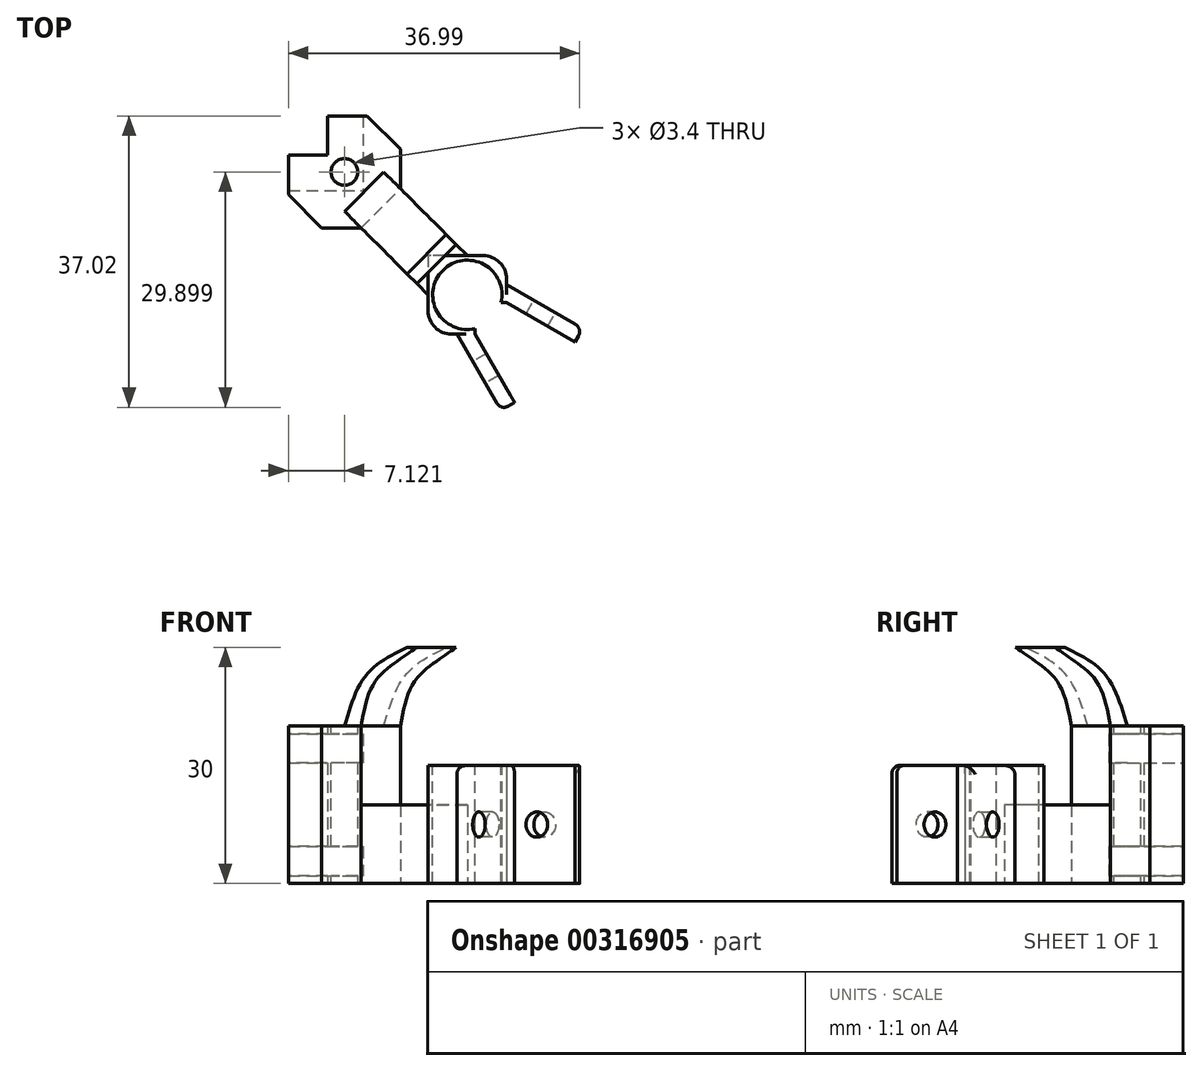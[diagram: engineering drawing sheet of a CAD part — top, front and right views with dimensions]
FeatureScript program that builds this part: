
annotation { "Feature Type Name" : "Feature", "Feature Type Description" : "" }
export const myFeature = defineFeature(function(context is Context, id is Id, definition is map)
    precondition{}
    {
        {
            var Q0;
            Q0=qCreatedBy(makeId("Top.planeOp"),FACE);
            var sketch = newSketch(context, id + "F0", { "sketchPlane" : qUnion([Q0])});
            skLineSegment(sketch, "E0", {"start": v(0, 0) * mm, "end": v(-5, 0) * mm});
            skLineSegment(sketch, "E1", {"start": v(-5, 0) * mm, "end": v(-5, 5) * mm});
            skLineSegment(sketch, "E2", {"start": v(-5, 5) * mm, "end": v(0, 5) * mm});
            skLineSegment(sketch, "E3", {"start": v(0, 5) * mm, "end": v(0, 10) * mm});
            skLineSegment(sketch, "E4", {"start": v(0, 10) * mm, "end": v(5, 10) * mm});
            skLineSegment(sketch, "E5", {"start": v(5, 10) * mm, "end": v(5, 5) * mm});
            skLineSegment(sketch, "E6", {"start": v(-5, 0) * mm, "end": v(-0.76, -4.24) * mm});
            skLineSegment(sketch, "E7", {"start": v(5, 10) * mm, "end": v(9.24, 5.76) * mm});
            skLineSegment(sketch, "E8", {"start": v(9.24, 5.76) * mm, "end": v(9.24, 0.76) * mm});
            skLineSegment(sketch, "E9", {"start": v(-0.76, -4.24) * mm, "end": v(4.24, -4.24) * mm});
            skLineSegment(sketch, "E10", {"start": v(9.24, 0.76) * mm, "end": v(17.73, -7.73) * mm});
            skLineSegment(sketch, "E11", {"start": v(4.24, -4.24) * mm, "end": v(12.73, -12.73) * mm});
            skLineSegment(sketch, "E12", {"start": v(12.73, -12.73) * mm, "end": v(12.73, -17.73) * mm});
            skLineSegment(sketch, "E13", {"start": v(12.73, -17.73) * mm, "end": v(22.73, -17.73) * mm});
            skLineSegment(sketch, "E14", {"start": v(22.73, -17.73) * mm, "end": v(22.73, -7.73) * mm});
            skLineSegment(sketch, "E15", {"start": v(22.73, -7.73) * mm, "end": v(17.73, -7.73) * mm});
            skLineSegment(sketch, "E16", {"start": v(4.24, -4.24) * mm, "end": v(9.24, 0.76) * mm});
            skPoint(sketch, "E17", {"position": v(22.73, -13.73) * mm});
            skPoint(sketch, "E18", {"position": v(18.73, -17.73) * mm});
            skLineSegment(sketch, "E19", {"start": v(22.73, -13.73) * mm, "end": v(31.39, -18.73) * mm});
            skLineSegment(sketch, "E20", {"start": v(18.73, -17.73) * mm, "end": v(23.73, -26.39) * mm});
            skLineSegment(sketch, "E21", {"start": v(31.39, -18.73) * mm, "end": v(32.39, -17) * mm});
            skLineSegment(sketch, "E22", {"start": v(32.39, -17) * mm, "end": v(22.73, -11.42) * mm});
            skLineSegment(sketch, "E23", {"start": v(23.73, -26.39) * mm, "end": v(22, -27.39) * mm});
            skLineSegment(sketch, "E24", {"start": v(22, -27.39) * mm, "end": v(16.42, -17.73) * mm});
            skSolve(sketch);
        }
        {
            var Q0;
            Q0=makeQuery(id+"F0.imprint","IMPRINT",FACE,{"disambiguationData":[TD([[makeQuery(id+"F0.imprint","IMPRINT",EDGE,{"derivedFrom":sQuery(id+"F0.wireOp",EDGE,"E1")}),-1.0]])]});
            extrude(context, id + "F1", {"entities" : qUnion([Q0]), "depth" : 20 * mm});
        }
        {
            var Q0;
            Q0=makeQuery(id+"F0.imprint","IMPRINT",FACE,{"disambiguationData":[TD([[makeQuery(id+"F0.imprint","IMPRINT",EDGE,{"derivedFrom":sQuery(id+"F0.wireOp",EDGE,"E10")}),-1.0]])]});
            extrude(context, id + "F2", {"entities" : qUnion([Q0]), "operationType" : NewBodyOperationType.ADD, "depth" : 10 * mm});
        }
        {
            var Q0;
            Q0=makeQuery(id+"F1.opExtrude","SWEPT_FACE",FACE,{"disambiguationData":[OSD([sQuery(id+"F0.wireOp",EDGE,"E4")])]});
            var sketch = newSketch(context, id + "F3", { "sketchPlane" : qUnion([Q0])});
            skPoint(sketch, "E25", {"position": v(0, 19) * mm});
            skPoint(sketch, "E26", {"position": v(0, 15.6) * mm});
            skPoint(sketch, "E27", {"position": v(0, 1) * mm});
            skPoint(sketch, "E28", {"position": v(0, 4.4) * mm});
            skLineSegment(sketch, "E29", {"start": v(0, 19) * mm, "end": v(-5, 19) * mm});
            skLineSegment(sketch, "E30", {"start": v(-5, 19) * mm, "end": v(-5, 15.6) * mm});
            skLineSegment(sketch, "E31", {"start": v(-5, 15.6) * mm, "end": v(0, 15.6) * mm});
            skSolve(sketch);
        }
        {
            var Q0;
            Q0=qSketchRegion(id+"F3",true);
            var Q1;
            {var subQ0=sQuery(id+"F3.wireOp",EDGE,"E29");Q1=makeQuery(id+"F3.imprint","IMPRINT",FACE,{"disambiguationData":[TD([[makeQuery(id+"F3.imprint","IMPRINT",EDGE,{"derivedFrom":subQ0}),1.0]])]});}
            extrude(context, id + "F4", {"entities" : qUnion([Q0, Q1]), "operationType" : NewBodyOperationType.REMOVE, "oppositeDirection" : true, "depth" : 25 * mm});
        }
        {
            var Q0;
            Q0=makeQuery(id+"F1.opExtrude","SWEPT_FACE",FACE,{"disambiguationData":[OSD([sQuery(id+"F0.wireOp",EDGE,"E2")])]});
            var sketch = newSketch(context, id + "F5", { "sketchPlane" : qUnion([Q0])});
            skLineSegment(sketch, "E32", {"start": v(0, 19) * mm, "end": v(5, 19) * mm});
            skLineSegment(sketch, "E33", {"start": v(5, 19) * mm, "end": v(5, 15.6) * mm});
            skLineSegment(sketch, "E34", {"start": v(5, 15.6) * mm, "end": v(0, 15.6) * mm});
            skLineSegment(sketch, "E35", {"start": v(0, 15.6) * mm, "end": v(0, 19) * mm});
            skSolve(sketch);
        }
        {
            var Q0;
            Q0=makeQuery(id+"F5.imprint","IMPRINT",FACE,{"disambiguationData":[TD([[makeQuery(id+"F5.imprint","IMPRINT",EDGE,{"derivedFrom":sQuery(id+"F5.wireOp",EDGE,"E32")}),-1.0]])]});
            extrude(context, id + "F6", {"entities" : qUnion([Q0]), "operationType" : NewBodyOperationType.REMOVE, "oppositeDirection" : true, "depth" : 25 * mm});
        }
        {
            var Q0;
            Q0=makeQuery(id+"F1.opExtrude","SWEPT_FACE",FACE,{"disambiguationData":[OSD([sQuery(id+"F0.wireOp",EDGE,"E7")])]});
            var sketch = newSketch(context, id + "F7", { "sketchPlane" : qUnion([Q0])});
            skLineSegment(sketch, "E36", {"start": v(3.54, 15.6) * mm, "end": v(-2.46, 15.6) * mm});
            skLineSegment(sketch, "E37", {"start": v(-2.46, 15.6) * mm, "end": v(-2.46, 19) * mm});
            skLineSegment(sketch, "E38", {"start": v(-2.46, 19) * mm, "end": v(3.54, 19) * mm});
            skLineSegment(sketch, "E39", {"start": v(3.54, 19) * mm, "end": v(3.54, 15.6) * mm});
            skSolve(sketch);
        }
        {
            var Q0;
            Q0=qSketchRegion(id+"F7",true);
            extrude(context, id + "F8", {"entities" : qUnion([Q0]), "operationType" : NewBodyOperationType.REMOVE, "oppositeDirection" : true, "depth" : 25 * mm});
        }
        {
            var Q0;
            {var subQ3=sQuery(id+"F0.wireOp",EDGE,"E4");Q0=makeQuery(id+"F4.boolean.opBoolean","SPLIT",FACE,{"disambiguationData":[TD([makeQuery(id+"F4.opExtrude","SWEPT_FACE",FACE,{"disambiguationData":[OSD([sQuery(id+"F3.wireOp",EDGE,"E31")])]})])],"derivedFrom":makeQuery(id+"F1.opExtrude","SWEPT_FACE",FACE,{"disambiguationData":[OSD([subQ3])]})});}
            var sketch = newSketch(context, id + "F9", { "sketchPlane" : qUnion([Q0])});
            skPoint(sketch, "E40", {"position": v(0, 1) * mm});
            skPoint(sketch, "E41", {"position": v(0, 4.4) * mm});
            skLineSegment(sketch, "E42.bottom", {"start": v(0, 4.4) * mm, "end": v(-5, 4.4) * mm});
            skLineSegment(sketch, "E42.top", {"start": v(0, 1) * mm, "end": v(-5, 1) * mm});
            skLineSegment(sketch, "E42.left", {"start": v(0, 4.4) * mm, "end": v(0, 1) * mm});
            skLineSegment(sketch, "E42.right", {"start": v(-5, 4.4) * mm, "end": v(-5, 1) * mm});
            skSolve(sketch);
        }
        {
            var Q0;
            Q0=qSketchRegion(id+"F9",true);
            extrude(context, id + "F10", {"entities" : qUnion([Q0]), "operationType" : NewBodyOperationType.REMOVE, "oppositeDirection" : true, "depth" : 25 * mm});
        }
        {
            var Q0;
            {var subQ3=sQuery(id+"F0.wireOp",EDGE,"E7");Q0=makeQuery(id+"F8.boolean.opBoolean","SPLIT",FACE,{"disambiguationData":[TD([makeQuery(id+"F4.boolean.opBoolean","COPY",FACE,{"derivedFrom":makeQuery(id+"F4.opExtrude","SWEPT_FACE",FACE,{"disambiguationData":[OSD([sQuery(id+"F3.wireOp",EDGE,"E31")])]})})])],"derivedFrom":makeQuery(id+"F1.opExtrude","SWEPT_FACE",FACE,{"disambiguationData":[OSD([subQ3])]})});}
            var sketch = newSketch(context, id + "F11", { "sketchPlane" : qUnion([Q0])});
            skLineSegment(sketch, "E43.bottom", {"start": v(3.54, 1) * mm, "end": v(-2.46, 1) * mm});
            skLineSegment(sketch, "E43.top", {"start": v(3.54, 4.4) * mm, "end": v(-2.46, 4.4) * mm});
            skLineSegment(sketch, "E43.left", {"start": v(3.54, 1) * mm, "end": v(3.54, 4.4) * mm});
            skLineSegment(sketch, "E43.right", {"start": v(-2.46, 1) * mm, "end": v(-2.46, 4.4) * mm});
            skSolve(sketch);
        }
        {
            var Q0;
            Q0=qSketchRegion(id+"F11",true);
            extrude(context, id + "F12", {"entities" : qUnion([Q0]), "operationType" : NewBodyOperationType.REMOVE, "oppositeDirection" : true, "depth" : 25 * mm});
        }
        {
            var Q0;
            {var subQ2=sQuery(id+"F0.wireOp",EDGE,"E2");Q0=makeQuery(id+"F6.boolean.opBoolean","SPLIT",FACE,{"disambiguationData":[TD([makeQuery(id+"F4.boolean.opBoolean","COPY",FACE,{"derivedFrom":makeQuery(id+"F4.opExtrude","SWEPT_FACE",FACE,{"disambiguationData":[OSD([sQuery(id+"F3.wireOp",EDGE,"E31")])]})})])],"derivedFrom":makeQuery(id+"F1.opExtrude","SWEPT_FACE",FACE,{"disambiguationData":[OSD([subQ2])]})});}
            var sketch = newSketch(context, id + "F13", { "sketchPlane" : qUnion([Q0])});
            skLineSegment(sketch, "E44.bottom", {"start": v(0, 4.4) * mm, "end": v(5, 4.4) * mm});
            skLineSegment(sketch, "E44.top", {"start": v(0, 1) * mm, "end": v(5, 1) * mm});
            skLineSegment(sketch, "E44.left", {"start": v(0, 4.4) * mm, "end": v(0, 1) * mm});
            skLineSegment(sketch, "E44.right", {"start": v(5, 4.4) * mm, "end": v(5, 1) * mm});
            skSolve(sketch);
        }
        {
            var Q0;
            Q0=qSketchRegion(id+"F13",true);
            extrude(context, id + "F14", {"entities" : qUnion([Q0]), "operationType" : NewBodyOperationType.REMOVE, "oppositeDirection" : true, "depth" : 25 * mm});
        }
        {
            var Q0;
            Q0=makeQuery(id+"F1.opExtrude","CAP_FACE",FACE,{"disambiguationData":[OSD([sQuery(id+"F0.wireOp",EDGE,"E1"),sQuery(id+"F0.wireOp",EDGE,"E2"),sQuery(id+"F0.wireOp",EDGE,"E3"),sQuery(id+"F0.wireOp",EDGE,"E4"),sQuery(id+"F0.wireOp",EDGE,"E6"),sQuery(id+"F0.wireOp",EDGE,"E7"),sQuery(id+"F0.wireOp",EDGE,"E8"),sQuery(id+"F0.wireOp",EDGE,"E9"),sQuery(id+"F0.wireOp",EDGE,"E16")])],"isStart":false});
            var sketch = newSketch(context, id + "F15", { "sketchPlane" : qUnion([Q0])});
            skLineSegment(sketch, "E45", {"start": v(0, 5) * mm, "end": v(0, 3.17) * mm});
            skLineSegment(sketch, "E46", {"start": v(0, 5) * mm, "end": v(2.05, 5) * mm});
            skLineSegment(sketch, "E47", {"start": v(0, 5) * mm, "end": v(2.12, 2.88) * mm});
            skSolve(sketch);
        }
        {
            var Q0;
            Q0=sQuery(id+"F15.wireOp",VERTEX,"E47.end");
            var Q1;
            Q1=makeQuery(id+"F1.opExtrude","SWEPT_BODY",BODY,{"disambiguationData":[OSD([sQuery(id+"F0.wireOp",EDGE,"E1"),sQuery(id+"F0.wireOp",EDGE,"E2"),sQuery(id+"F0.wireOp",EDGE,"E3"),sQuery(id+"F0.wireOp",EDGE,"E4"),sQuery(id+"F0.wireOp",EDGE,"E6"),sQuery(id+"F0.wireOp",EDGE,"E7"),sQuery(id+"F0.wireOp",EDGE,"E8"),sQuery(id+"F0.wireOp",EDGE,"E9"),sQuery(id+"F0.wireOp",EDGE,"E16")])]});
            hole(context, id + "F16", {"style" : HoleStyle.SIMPLE, "endStyle" : HoleEndStyle.THROUGH, "holeDiameter" : 3.4 * mm, "tappedDepth" : 12 * mm, "tapClearance" : 3, "locations" : qUnion([Q0]), "scope" : qUnion([Q1])});
        }
        {
            var Q0;
            Q0=makeQuery(id+"F2.opExtrude","CAP_FACE",FACE,{"disambiguationData":[OSD([sQuery(id+"F0.wireOp",EDGE,"E10"),sQuery(id+"F0.wireOp",EDGE,"E11"),sQuery(id+"F0.wireOp",EDGE,"E12"),sQuery(id+"F0.wireOp",EDGE,"E13"),sQuery(id+"F0.wireOp",EDGE,"E14"),sQuery(id+"F0.wireOp",EDGE,"E15"),sQuery(id+"F0.wireOp",EDGE,"E16")])],"isStart":false});
            var sketch = newSketch(context, id + "F17", { "sketchPlane" : qUnion([Q0])});
            skLineSegment(sketch, "E48", {"start": v(22.73, -7.73) * mm, "end": v(12.73, -17.73) * mm});
            skLineSegment(sketch, "E49", {"start": v(22.73, -17.73) * mm, "end": v(13.62, -8.62) * mm});
            skPoint(sketch, "E50", {"position": v(17.73, -12.73) * mm});
            skSolve(sketch);
        }
        {
            var Q0;
            Q0=sQuery(id+"F17.wireOp",VERTEX,"E50");
            var Q1;
            Q1=makeQuery(id+"F1.opExtrude","SWEPT_BODY",BODY,{"disambiguationData":[OSD([sQuery(id+"F0.wireOp",EDGE,"E1"),sQuery(id+"F0.wireOp",EDGE,"E2"),sQuery(id+"F0.wireOp",EDGE,"E3"),sQuery(id+"F0.wireOp",EDGE,"E4"),sQuery(id+"F0.wireOp",EDGE,"E6"),sQuery(id+"F0.wireOp",EDGE,"E7"),sQuery(id+"F0.wireOp",EDGE,"E8"),sQuery(id+"F0.wireOp",EDGE,"E9"),sQuery(id+"F0.wireOp",EDGE,"E16")])]});
            hole(context, id + "F18", {"style" : HoleStyle.SIMPLE, "endStyle" : HoleEndStyle.THROUGH, "holeDiameter" : 8.8 * mm, "tappedDepth" : 12 * mm, "tapClearance" : 3, "locations" : qUnion([Q0]), "scope" : qUnion([Q1])});
        }
        {
            var Q0;
            Q0=makeQuery(id+"F2.opExtrude","CAP_FACE",FACE,{"disambiguationData":[OSD([sQuery(id+"F0.wireOp",EDGE,"E10"),sQuery(id+"F0.wireOp",EDGE,"E11"),sQuery(id+"F0.wireOp",EDGE,"E12"),sQuery(id+"F0.wireOp",EDGE,"E13"),sQuery(id+"F0.wireOp",EDGE,"E14"),sQuery(id+"F0.wireOp",EDGE,"E15"),sQuery(id+"F0.wireOp",EDGE,"E16")])],"isStart":false});
            var sketch = newSketch(context, id + "F19", { "sketchPlane" : qUnion([Q0])});
            skLineSegment(sketch, "E51.bottom", {"start": v(22.73, -7.73) * mm, "end": v(12.73, -7.73) * mm});
            skLineSegment(sketch, "E51.top", {"start": v(22.73, -17.73) * mm, "end": v(12.73, -17.73) * mm});
            skLineSegment(sketch, "E51.left", {"start": v(22.73, -7.73) * mm, "end": v(22.73, -17.73) * mm});
            skLineSegment(sketch, "E51.right", {"start": v(12.73, -7.73) * mm, "end": v(12.73, -17.73) * mm});
            skSolve(sketch);
        }
        {
            var Q0;
            {var subQ1=sQuery(id+"F19.wireOp",EDGE,"E51.top");Q0=makeQuery(id+"F19.imprint","IMPRINT",FACE,{"disambiguationData":[TD([[makeQuery(id+"F19.imprint","IMPRINT",EDGE,{"derivedFrom":subQ1}),1.0]])]});}
            extrude(context, id + "F20", {"entities" : qUnion([Q0]), "operationType" : NewBodyOperationType.ADD, "depth" : 5 * mm});
        }
        {
            var Q0;
            Q0=makeQuery(id+"F8.boolean.opBoolean","MERGE",FACE,{"derivedFrom":[makeQuery(id+"F6.boolean.opBoolean","MERGE",FACE,{"derivedFrom":[makeQuery(id+"F4.boolean.opBoolean","COPY",FACE,{"derivedFrom":makeQuery(id+"F4.opExtrude","SWEPT_FACE",FACE,{"disambiguationData":[OSD([sQuery(id+"F3.wireOp",EDGE,"E31")])]})}),makeQuery(id+"F6.opExtrude","SWEPT_FACE",FACE,{"disambiguationData":[OSD([sQuery(id+"F5.wireOp",EDGE,"E34")])]})]}),makeQuery(id+"F8.opExtrude","SWEPT_FACE",FACE,{"disambiguationData":[OSD([sQuery(id+"F7.wireOp",EDGE,"E36")])]})]});
            extrude(context, id + "F21", {"entities" : qUnion([Q0]), "operationType" : NewBodyOperationType.REMOVE, "oppositeDirection" : true, "depth" : 0.3 * mm});
        }
        {
            var Q0;
            Q0=makeQuery(id+"F14.boolean.opBoolean","MERGE",FACE,{"derivedFrom":[makeQuery(id+"F12.boolean.opBoolean","MERGE",FACE,{"derivedFrom":[makeQuery(id+"F10.boolean.opBoolean","COPY",FACE,{"derivedFrom":makeQuery(id+"F10.opExtrude","SWEPT_FACE",FACE,{"disambiguationData":[OSD([sQuery(id+"F9.wireOp",EDGE,"E42.bottom")])]})}),makeQuery(id+"F12.opExtrude","SWEPT_FACE",FACE,{"disambiguationData":[OSD([sQuery(id+"F11.wireOp",EDGE,"E43.top")])]})]}),makeQuery(id+"F14.opExtrude","SWEPT_FACE",FACE,{"disambiguationData":[OSD([sQuery(id+"F13.wireOp",EDGE,"E44.bottom")])]})]});
            extrude(context, id + "F22", {"entities" : qUnion([Q0]), "operationType" : NewBodyOperationType.REMOVE, "oppositeDirection" : true, "depth" : 0.3 * mm});
        }
        {
            var Q0;
            Q0=makeQuery(id+"F20.boolean.opBoolean","MERGE",FACE,{"derivedFrom":[makeQuery(id+"F2.opExtrude","SWEPT_FACE",FACE,{"disambiguationData":[OSD([sQuery(id+"F0.wireOp",EDGE,"E13")])]}),makeQuery(id+"F20.opExtrude","SWEPT_FACE",FACE,{"disambiguationData":[OSD([sQuery(id+"F19.wireOp",EDGE,"E51.top")])]})]});
            var sketch = newSketch(context, id + "F23", { "sketchPlane" : qUnion([Q0])});
            skLineSegment(sketch, "E52", {"start": v(12.79, 15) * mm, "end": v(22.73, 15) * mm});
            skPoint(sketch, "E53", {"position": v(18.73, 15) * mm});
            skLineSegment(sketch, "E54", {"start": v(18.73, 15) * mm, "end": v(18.73, 0) * mm});
            skLineSegment(sketch, "E55", {"start": v(18.73, 0) * mm, "end": v(22.73, 0) * mm});
            skLineSegment(sketch, "E56", {"start": v(22.73, 0) * mm, "end": v(22.73, 15) * mm});
            skSolve(sketch);
        }
        {
            var Q0;
            Q0=makeQuery(id+"F20.boolean.opBoolean","MERGE",FACE,{"derivedFrom":[makeQuery(id+"F2.opExtrude","SWEPT_FACE",FACE,{"disambiguationData":[OSD([sQuery(id+"F0.wireOp",EDGE,"E14")])]}),makeQuery(id+"F20.opExtrude","SWEPT_FACE",FACE,{"disambiguationData":[OSD([sQuery(id+"F19.wireOp",EDGE,"E51.left")])]})]});
            var sketch = newSketch(context, id + "F24", { "sketchPlane" : qUnion([Q0])});
            skLineSegment(sketch, "E57", {"start": v(-17.73, 15) * mm, "end": v(-7.73, 15) * mm});
            skPoint(sketch, "E58", {"position": v(-13.73, 15) * mm});
            skLineSegment(sketch, "E59", {"start": v(-13.73, 15) * mm, "end": v(-13.73, 0) * mm});
            skLineSegment(sketch, "E60", {"start": v(-13.73, 0) * mm, "end": v(-17.73, 0) * mm});
            skLineSegment(sketch, "E61", {"start": v(-17.73, 0) * mm, "end": v(-17.73, 15) * mm});
            skSolve(sketch);
        }
        {
            var Q0;
            Q0=qSketchRegion(id+"F24",true);
            extrude(context, id + "F25", {"entities" : qUnion([Q0]), "operationType" : NewBodyOperationType.REMOVE, "oppositeDirection" : true, "depth" : 2.4 * mm});
        }
        {
            var Q0;
            Q0=qSketchRegion(id+"F23",true);
            extrude(context, id + "F26", {"entities" : qUnion([Q0]), "operationType" : NewBodyOperationType.REMOVE, "oppositeDirection" : true, "depth" : 3.85 * mm});
        }
        {
            var Q0;
            Q0=makeQuery(id+"F20.boolean.opBoolean","MERGE",EDGE,{"derivedFrom":[makeQuery(id+"F2.opExtrude","SWEPT_EDGE",EDGE,{"disambiguationData":[OSD([sQuery(id+"F0.wireOp",EDGE,"E14"),sQuery(id+"F0.wireOp",EDGE,"E15")])]}),makeQuery(id+"F20.opExtrude","SWEPT_EDGE",EDGE,{"disambiguationData":[OSD([sQuery(id+"F19.wireOp",EDGE,"E51.bottom"),sQuery(id+"F19.wireOp",EDGE,"E51.left")])]})]});
            fillet(context, id + "F27", {"entities" : qUnion([Q0]), "radius" : 3 * mm, "tangentPropagation" : true, "allowEdgeOverflow" : false});
        }
        {
            var Q0;
            Q0=makeQuery(id+"F20.boolean.opBoolean","MERGE",EDGE,{"derivedFrom":[makeQuery(id+"F2.opExtrude","SWEPT_EDGE",EDGE,{"disambiguationData":[OSD([sQuery(id+"F0.wireOp",EDGE,"E12"),sQuery(id+"F0.wireOp",EDGE,"E13")])]}),makeQuery(id+"F20.opExtrude","SWEPT_EDGE",EDGE,{"disambiguationData":[OSD([sQuery(id+"F19.wireOp",EDGE,"E51.top"),sQuery(id+"F19.wireOp",EDGE,"E51.right")])]})]});
            fillet(context, id + "F28", {"entities" : qUnion([Q0]), "radius" : 3 * mm, "tangentPropagation" : true, "allowEdgeOverflow" : false});
        }
        {
            var Q0;
            Q0=makeQuery(id+"F21.boolean.opBoolean","COPY",FACE,{"derivedFrom":makeQuery(id+"F21.opExtrude","CAP_FACE",FACE,{"disambiguationData":[OSD([sQuery(id+"F3.wireOp",EDGE,"E31"),sQuery(id+"F5.wireOp",EDGE,"E34"),sQuery(id+"F7.wireOp",EDGE,"E36")])],"isStart":false})});
            var sketch = newSketch(context, id + "F29", { "sketchPlane" : qUnion([Q0])});
            skLineSegment(sketch, "E62", {"start": v(4.45, 0.55) * mm, "end": v(-5, 0.55) * mm});
            skLineSegment(sketch, "E63", {"start": v(4.45, 0.55) * mm, "end": v(4.45, 10) * mm});
            skSolve(sketch);
        }
        {
            var Q0;
            {var subQ6=sQuery(id+"F29.wireOp",EDGE,"E62");Q0=makeQuery(id+"F29.imprint","IMPRINT",FACE,{"disambiguationData":[TD([[makeQuery(id+"F29.imprint","IMPRINT",EDGE,{"derivedFrom":subQ6}),1.0]])]});}
            extrude(context, id + "F30", {"entities" : qUnion([Q0]), "operationType" : NewBodyOperationType.ADD, "depth" : 4 * mm, "hasSecondDirection" : true, "secondDirectionOppositeDirection" : true, "secondDirectionDepth" : 14.72 * mm});
        }
        {
            var Q0;
            {var subQ1=sQuery(id+"F0.wireOp",EDGE,"E9");Q0=makeQuery(id+"F30.boolean.opBoolean","SPLIT",FACE,{"disambiguationData":[TD([makeQuery(id+"F1.opExtrude","SWEPT_FACE",FACE,{"disambiguationData":[OSD([subQ1])]})])],"derivedFrom":makeQuery(id+"F14.boolean.opBoolean","MERGE",FACE,{"derivedFrom":[makeQuery(id+"F12.boolean.opBoolean","MERGE",FACE,{"derivedFrom":[makeQuery(id+"F10.boolean.opBoolean","COPY",FACE,{"derivedFrom":makeQuery(id+"F10.opExtrude","SWEPT_FACE",FACE,{"disambiguationData":[OSD([sQuery(id+"F9.wireOp",EDGE,"E42.top")])]})}),makeQuery(id+"F12.opExtrude","SWEPT_FACE",FACE,{"disambiguationData":[OSD([sQuery(id+"F11.wireOp",EDGE,"E43.bottom")])]})]}),makeQuery(id+"F14.opExtrude","SWEPT_FACE",FACE,{"disambiguationData":[OSD([sQuery(id+"F13.wireOp",EDGE,"E44.top")])]})]})});}
            extrude(context, id + "F31", {"entities" : qUnion([Q0]), "operationType" : NewBodyOperationType.ADD, "depth" : 4.73 * mm});
        }
        {
            var Q0;
            {var subQ0=sQuery(id+"F0.wireOp",EDGE,"E20");Q0=makeQuery(id+"F0.imprint","IMPRINT",FACE,{"disambiguationData":[TD([[makeQuery(id+"F0.imprint","IMPRINT",EDGE,{"derivedFrom":subQ0}),-1.0]])]});}
            var Q1;
            {var subQ0=sQuery(id+"F0.wireOp",EDGE,"E19");Q1=makeQuery(id+"F0.imprint","IMPRINT",FACE,{"disambiguationData":[TD([[makeQuery(id+"F0.imprint","IMPRINT",EDGE,{"derivedFrom":subQ0}),1.0]])]});}
            extrude(context, id + "F32", {"entities" : qUnion([Q0, Q1]), "operationType" : NewBodyOperationType.ADD, "depth" : 15 * mm});
        }
        {
            var Q0;
            Q0=makeQuery(id+"F32.opExtrude","SWEPT_FACE",FACE,{"disambiguationData":[OSD([sQuery(id+"F0.wireOp",EDGE,"E22")])]});
            var sketch = newSketch(context, id + "F33", { "sketchPlane" : qUnion([Q0])});
            skLineSegment(sketch, "E64", {"start": v(-25.4, 15) * mm, "end": v(-36.55, 0) * mm});
            skLineSegment(sketch, "E65", {"start": v(-36.55, 15) * mm, "end": v(-25.4, 0) * mm});
            skPoint(sketch, "E66", {"position": v(-30.97, 7.5) * mm});
            skSolve(sketch);
        }
        {
            var Q0;
            Q0=sQuery(id+"F33.wireOp",VERTEX,"E66");
            var Q1;
            Q1=makeQuery(id+"F1.opExtrude","SWEPT_BODY",BODY,{"disambiguationData":[OSD([sQuery(id+"F0.wireOp",EDGE,"E1"),sQuery(id+"F0.wireOp",EDGE,"E2"),sQuery(id+"F0.wireOp",EDGE,"E3"),sQuery(id+"F0.wireOp",EDGE,"E4"),sQuery(id+"F0.wireOp",EDGE,"E6"),sQuery(id+"F0.wireOp",EDGE,"E7"),sQuery(id+"F0.wireOp",EDGE,"E8"),sQuery(id+"F0.wireOp",EDGE,"E9"),sQuery(id+"F0.wireOp",EDGE,"E16")])]});
            hole(context, id + "F34", {"style" : HoleStyle.SIMPLE, "endStyle" : HoleEndStyle.BLIND, "holeDiameter" : 3.2 * mm, "holeDepth" : 5 * mm, "tappedDepth" : 12 * mm, "tapClearance" : 3, "locations" : qUnion([Q0]), "scope" : qUnion([Q1])});
        }
        {
            var Q0;
            Q0=makeQuery(id+"F32.opExtrude","SWEPT_FACE",FACE,{"disambiguationData":[OSD([sQuery(id+"F0.wireOp",EDGE,"E24")])]});
            var sketch = newSketch(context, id + "F35", { "sketchPlane" : qUnion([Q0])});
            skLineSegment(sketch, "E67", {"start": v(23.56, 15) * mm, "end": v(34.72, 0) * mm});
            skLineSegment(sketch, "E68", {"start": v(34.72, 15) * mm, "end": v(23.56, 0) * mm});
            skPoint(sketch, "E69", {"position": v(29.14, 7.5) * mm});
            skSolve(sketch);
        }
        {
            var Q0;
            Q0=sQuery(id+"F35.wireOp",VERTEX,"E69");
            var Q1;
            Q1=makeQuery(id+"F1.opExtrude","SWEPT_BODY",BODY,{"disambiguationData":[OSD([sQuery(id+"F0.wireOp",EDGE,"E1"),sQuery(id+"F0.wireOp",EDGE,"E2"),sQuery(id+"F0.wireOp",EDGE,"E3"),sQuery(id+"F0.wireOp",EDGE,"E4"),sQuery(id+"F0.wireOp",EDGE,"E6"),sQuery(id+"F0.wireOp",EDGE,"E7"),sQuery(id+"F0.wireOp",EDGE,"E8"),sQuery(id+"F0.wireOp",EDGE,"E9"),sQuery(id+"F0.wireOp",EDGE,"E16")])]});
            hole(context, id + "F36", {"style" : HoleStyle.SIMPLE, "endStyle" : HoleEndStyle.BLIND, "holeDiameter" : 3.2 * mm, "holeDepth" : 5 * mm, "tappedDepth" : 12 * mm, "tapClearance" : 3, "locations" : qUnion([Q0]), "scope" : qUnion([Q1])});
        }
        {
            var Q0;
            Q0=makeQuery(id+"F32.opExtrude","CAP_EDGE",EDGE,{"disambiguationData":[OSD([sQuery(id+"F0.wireOp",EDGE,"E24")])],"isStart":false});
            fillet(context, id + "F37", {"entities" : qUnion([Q0]), "radius" : 1 * mm, "tangentPropagation" : true, "allowEdgeOverflow" : false});
        }
        {
            var Q0;
            Q0=makeQuery(id+"F32.opExtrude","SWEPT_EDGE",EDGE,{"disambiguationData":[OSD([sQuery(id+"F0.wireOp",EDGE,"E23"),sQuery(id+"F0.wireOp",EDGE,"E24")])]});
            fillet(context, id + "F38", {"entities" : qUnion([Q0]), "radius" : 1 * mm, "tangentPropagation" : true, "allowEdgeOverflow" : false});
        }
        {
            var Q0;
            Q0=makeQuery(id+"F32.opExtrude","CAP_EDGE",EDGE,{"disambiguationData":[OSD([sQuery(id+"F0.wireOp",EDGE,"E22")])],"isStart":false});
            var Q1;
            Q1=makeQuery(id+"F32.opExtrude","SWEPT_EDGE",EDGE,{"disambiguationData":[OSD([sQuery(id+"F0.wireOp",EDGE,"E21"),sQuery(id+"F0.wireOp",EDGE,"E22")])]});
            fillet(context, id + "F39", {"entities" : qUnion([Q0, Q1]), "radius" : 1.1 * mm, "tangentPropagation" : true, "allowEdgeOverflow" : false});
        }
        {
            var Q0;
            Q0=makeQuery(id+"F1.opExtrude","CAP_FACE",FACE,{"disambiguationData":[OSD([sQuery(id+"F0.wireOp",EDGE,"E1"),sQuery(id+"F0.wireOp",EDGE,"E2"),sQuery(id+"F0.wireOp",EDGE,"E3"),sQuery(id+"F0.wireOp",EDGE,"E4"),sQuery(id+"F0.wireOp",EDGE,"E6"),sQuery(id+"F0.wireOp",EDGE,"E7"),sQuery(id+"F0.wireOp",EDGE,"E8"),sQuery(id+"F0.wireOp",EDGE,"E9"),sQuery(id+"F0.wireOp",EDGE,"E16")])],"isStart":false});
            var sketch = newSketch(context, id + "F40", { "sketchPlane" : qUnion([Q0])});
            skLineSegment(sketch, "E70", {"start": v(9.24, 0.76) * mm, "end": v(7.12, 2.88) * mm});
            skLineSegment(sketch, "E71", {"start": v(4.24, -4.24) * mm, "end": v(2.12, -2.12) * mm});
            skLineSegment(sketch, "E72", {"start": v(2.12, -2.12) * mm, "end": v(7.12, 2.88) * mm});
            skLineSegment(sketch, "E73", {"start": v(9.24, 0.76) * mm, "end": v(4.24, -4.24) * mm});
            skSolve(sketch);
        }
        {
            var Q0;
            Q0=makeQuery(id+"F40.imprint","IMPRINT",FACE,{"disambiguationData":[TD([[makeQuery(id+"F40.imprint","IMPRINT",EDGE,{"derivedFrom":sQuery(id+"F40.wireOp",EDGE,"E70")}),1.0]])]});
            extrude(context, id + "F41", {"entities" : qUnion([Q0]), "operationType" : NewBodyOperationType.ADD, "depth" : 10 * mm});
        }
        {
            var Q0;
            {var subQ0=sQuery(id+"F0.wireOp",EDGE,"E16");Q0=makeQuery(id+"F41.boolean.opBoolean","MERGE",FACE,{"derivedFrom":[makeQuery(id+"F30.boolean.opBoolean","MERGE",FACE,{"derivedFrom":[makeQuery(id+"F1.opExtrude","SWEPT_FACE",FACE,{"disambiguationData":[OSD([subQ0])]}),makeQuery(id+"F30.opExtrude","SWEPT_FACE",FACE,{"disambiguationData":[OSD([subQ0,sQuery(id+"F3.wireOp",EDGE,"E31")])]})]}),makeQuery(id+"F41.opExtrude","SWEPT_FACE",FACE,{"disambiguationData":[OSD([sQuery(id+"F40.wireOp",EDGE,"E73")])]})]});}
            var sketch = newSketch(context, id + "F42", { "sketchPlane" : qUnion([Q0])});
            skLineSegment(sketch, "E74", {"start": v(7.07, 30) * mm, "end": v(0, 30) * mm});
            skLineSegment(sketch, "E75", {"start": v(0, 30) * mm, "end": v(0, 20) * mm});
            skLineSegment(sketch, "E76", {"start": v(0, 20) * mm, "end": v(7.07, 20) * mm});
            skLineSegment(sketch, "E77", {"start": v(7.07, 20) * mm, "end": v(7.07, 30) * mm});
            skSolve(sketch);
        }
        {
            var Q0;
            Q0=makeQuery(id+"F42.imprint","IMPRINT",FACE,{"disambiguationData":[TD([[makeQuery(id+"F42.imprint","IMPRINT",EDGE,{"derivedFrom":sQuery(id+"F42.wireOp",EDGE,"E74")}),-1.0]])]});
            extrude(context, id + "F43", {"entities" : qUnion([Q0]), "operationType" : NewBodyOperationType.ADD, "depth" : 10 * mm});
        }
        {
            var Q0;
            Q0=makeQuery(id+"F43.boolean.opBoolean","MERGE",FACE,{"derivedFrom":[makeQuery(id+"F41.opExtrude","SWEPT_FACE",FACE,{"disambiguationData":[OSD([sQuery(id+"F40.wireOp",EDGE,"E71")])]}),makeQuery(id+"F43.opExtrude","SWEPT_FACE",FACE,{"disambiguationData":[OSD([sQuery(id+"F42.wireOp",EDGE,"E75")])]})]});
            var sketch = newSketch(context, id + "F44", { "sketchPlane" : qUnion([Q0])});
            skFitSpline(sketch, "E78", {"points": [v(3, 20) * mm, v(6.71, 26.31) * mm, v(14.22, 30) * mm], "startDerivative": vector(6.03, 14.5) * mm, "endDerivative": vector(16.3, 5.6) * mm});
            skFitSpline(sketch, "E79", {"points": [v(16, 30) * mm, v(12.63, 28.32) * mm, v(8.24, 25.38) * mm, v(6, 20) * mm], "startDerivative": vector(-10.89, -5.46) * mm, "endDerivative": vector(-4.29, -16.36) * mm});
            skLineSegment(sketch, "E80", {"start": v(14.22, 30) * mm, "end": v(16, 30) * mm});
            skSolve(sketch);
        }
        {
            var Q0;
            {var subQ0=sQuery(id+"F44.wireOp",EDGE,"E78");Q0=makeQuery(id+"F44.imprint","IMPRINT",FACE,{"disambiguationData":[TD([[makeQuery(id+"F44.imprint","IMPRINT",EDGE,{"derivedFrom":subQ0}),1.0]])]});}
            var Q1;
            Q1=makeQuery(id+"F44.imprint","IMPRINT",FACE,{"disambiguationData":[TD([[makeQuery(id+"F44.imprint","IMPRINT",EDGE,{"derivedFrom":sQuery(id+"F44.wireOp",EDGE,"E79")}),1.0]])]});
            extrude(context, id + "F45", {"entities" : qUnion([Q0, Q1]), "operationType" : NewBodyOperationType.REMOVE, "oppositeDirection" : true, "depth" : 25 * mm});
        }
    });
